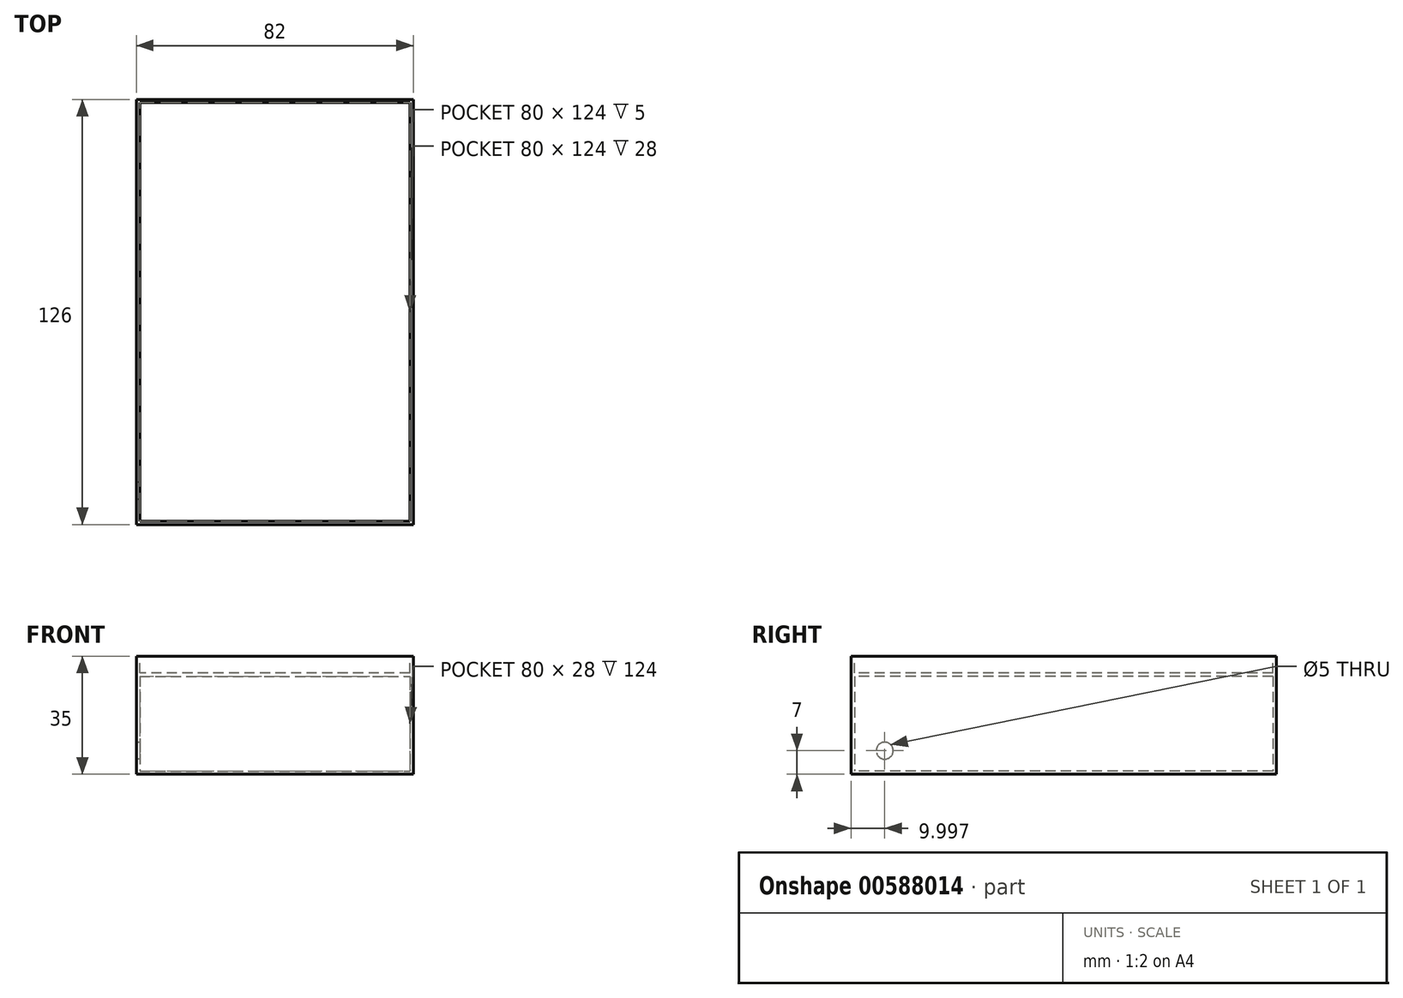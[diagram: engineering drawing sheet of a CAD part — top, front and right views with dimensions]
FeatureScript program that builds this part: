
annotation { "Feature Type Name" : "Feature", "Feature Type Description" : "" }
export const myFeature = defineFeature(function(context is Context, id is Id, definition is map)
    precondition{}
    {
        {
            var Q0;
            Q0=qCreatedBy(makeId("Top.planeOp"),FACE);
            var sketch = newSketch(context, id + "F0", { "sketchPlane" : qUnion([Q0])});
            skLineSegment(sketch, "E0.bottom", {"start": v(-41.27, 62.47) * mm, "end": v(40.73, 62.47) * mm});
            skLineSegment(sketch, "E0.top", {"start": v(-41.27, -63.53) * mm, "end": v(40.73, -63.53) * mm});
            skLineSegment(sketch, "E0.left", {"start": v(-41.27, 62.47) * mm, "end": v(-41.27, -63.53) * mm});
            skLineSegment(sketch, "E0.right", {"start": v(40.73, 62.47) * mm, "end": v(40.73, -63.53) * mm});
            skSolve(sketch);
        }
        {
            var Q0;
            Q0 = qSketchRegion(id + "F0", true);
            extrude(context, id + "F1", {"entities" : qUnion([Q0]), "depth" : 35 * mm, "offsetDistance" : 25 * mm});
        }
        {
            var Q0;
            Q0=makeQuery(id+"F1.opExtrude","CAP_FACE",FACE,{"disambiguationData":[OSD([sQuery(id+"F0.wireOp",EDGE,"E0.bottom"),sQuery(id+"F0.wireOp",EDGE,"E0.top"),sQuery(id+"F0.wireOp",EDGE,"E0.left"),sQuery(id+"F0.wireOp",EDGE,"E0.right")])],"isStart":false});
            var sketch = newSketch(context, id + "F2", { "sketchPlane" : qUnion([Q0])});
            skLineSegment(sketch, "E1.0", {"start": v(-40.27, 61.47) * mm, "end": v(-40.27, -62.53) * mm});
            skLineSegment(sketch, "E1.1", {"start": v(39.73, 61.47) * mm, "end": v(-40.27, 61.47) * mm});
            skLineSegment(sketch, "E1.2", {"start": v(39.73, -62.53) * mm, "end": v(39.73, 61.47) * mm});
            skLineSegment(sketch, "E1.3", {"start": v(-40.27, -62.53) * mm, "end": v(39.73, -62.53) * mm});
            skSolve(sketch);
        }
        {
            var Q0;
            Q0=makeQuery(id+"F2.imprint","IMPRINT",FACE,{"disambiguationData":[TD([[makeQuery(id+"F2.imprint","IMPRINT",EDGE,{"derivedFrom":sQuery(id+"F2.wireOp",EDGE,"E1.0")}),1.0]])]});
            extrude(context, id + "F3", {"entities" : qUnion([Q0]), "operationType" : NewBodyOperationType.REMOVE, "oppositeDirection" : true, "depth" : 5 * mm, "offsetDistance" : 25 * mm});
        }
        {
            var Q0;
            Q0=makeQuery(id+"F3.boolean.opBoolean","COPY",FACE,{"derivedFrom":makeQuery(id+"F3.opExtrude","CAP_FACE",FACE,{"disambiguationData":[OSD([sQuery(id+"F2.wireOp",EDGE,"E1.0"),sQuery(id+"F2.wireOp",EDGE,"E1.1"),sQuery(id+"F2.wireOp",EDGE,"E1.2"),sQuery(id+"F2.wireOp",EDGE,"E1.3")])],"isStart":false})});
            extrude(context, id + "F4", {"entities" : qUnion([Q0]), "operationType" : NewBodyOperationType.ADD, "depth" : -1 * mm, "offsetDistance" : 25 * mm});
        }
        {
            var Q0;
            Q0=makeQuery(id+"F3.boolean.opBoolean","COPY",FACE,{"derivedFrom":makeQuery(id+"F3.opExtrude","CAP_FACE",FACE,{"disambiguationData":[OSD([sQuery(id+"F2.wireOp",EDGE,"E1.0"),sQuery(id+"F2.wireOp",EDGE,"E1.1"),sQuery(id+"F2.wireOp",EDGE,"E1.2"),sQuery(id+"F2.wireOp",EDGE,"E1.3")])],"isStart":false})});
            var Q1;
            Q1=makeQuery(id+"F1.opExtrude","SWEPT_BODY",BODY,{"disambiguationData":[OSD([sQuery(id+"F0.wireOp",EDGE,"E0.bottom"),sQuery(id+"F0.wireOp",EDGE,"E0.top"),sQuery(id+"F0.wireOp",EDGE,"E0.left"),sQuery(id+"F0.wireOp",EDGE,"E0.right")])]});
            shell(context, id + "F5", {"isHollow" : true, "entities" : qUnion([Q0]), "parts" : qUnion([Q1]), "thickness" : 1 * mm});
        }
        {
            var Q0;
            Q0=makeQuery(id+"F1.opExtrude","SWEPT_FACE",FACE,{"disambiguationData":[OSD([sQuery(id+"F0.wireOp",EDGE,"E0.left")])]});
            var sketch = newSketch(context, id + "F6", { "sketchPlane" : qUnion([Q0])});
            skCircle(sketch, "E2", {"center": v(53.53, 7) * mm, "radius": 2.5 * mm});
            skSolve(sketch);
        }
        {
            var Q0;
            Q0=makeQuery(id+"F6.imprint","IMPRINT",FACE,{"disambiguationData":[TD([[makeQuery(id+"F6.imprint","IMPRINT",EDGE,{"derivedFrom":sQuery(id+"F6.wireOp",EDGE,"E2")}),1.0]])]});
            extrude(context, id + "F7", {"entities" : qUnion([Q0]), "operationType" : NewBodyOperationType.REMOVE, "oppositeDirection" : true, "depth" : 3 * mm, "offsetDistance" : 25 * mm});
        }
    });
